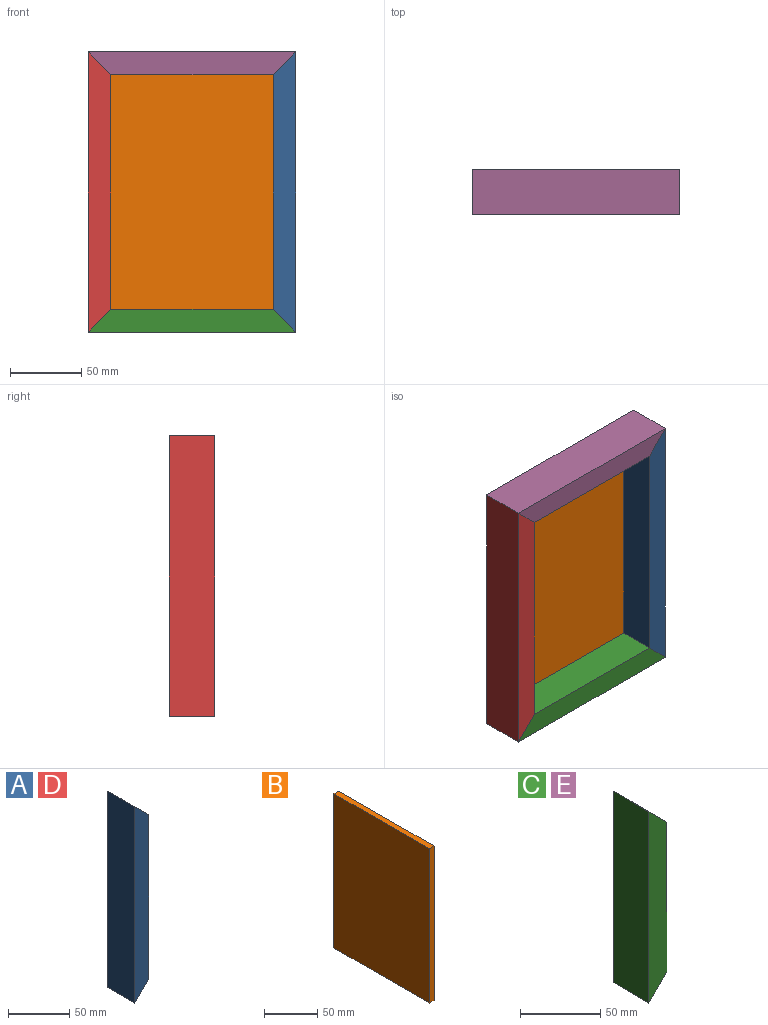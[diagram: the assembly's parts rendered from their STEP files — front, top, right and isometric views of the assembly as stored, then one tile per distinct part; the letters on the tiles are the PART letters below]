
ASSEMBLY  parts=5 mates=4
PART A: 8 faces, bbox 15.9x31.8x196.9 mm
  f0: plane 196.85x15.88mm, normal (0,-1,0), area 2873mm2, adj f1,f5,f6,f7
  f1: plane 165.1x25.4mm, normal (1,0,0), area 4193.5mm2, adj f0,f3,f6,f7
  f2: plane 196.85x9.53mm, normal (0,1,0), area 1784.3mm2, adj f4,f5,f6,f7
  f3: plane 177.8x6.35mm, normal (0,1,0), area 1088.7mm2, adj f1,f4,f6,f7
  f4: plane 177.8x6.35mm, normal (1,0,0), area 1129mm2, adj f2,f3,f6,f7
  f5: plane 196.85x31.75mm, normal (-1,0,0), area 6250mm2, adj f0,f2,f6,f7
  f6: plane 31.75x15.88mm, normal (0.71,0,-0.71), area 655.8mm2, adj f0,f1,f2,f3,f4,f5
  f7: plane 31.75x15.88mm, normal (0.71,0,0.71), area 655.8mm2, adj f0,f1,f2,f3,f4,f5
PART B: 6 faces, bbox 6.4x127x177.8 mm
  f0: plane 177.8x6.35mm, normal (0,1,0), area 1129mm2, adj f1,f3,f4,f5
  f1: plane 127x6.35mm, normal (0,0,1), area 806.5mm2, adj f0,f2,f4,f5
  f2: plane 177.8x6.35mm, normal (0,-1,0), area 1129mm2, adj f1,f3,f4,f5
  f3: plane 127x6.35mm, normal (0,0,-1), area 806.5mm2, adj f0,f2,f4,f5
  f4: plane 177.8x127mm, normal (1,0,0), area 22580.6mm2, adj f0,f1,f2,f3
  f5: plane 177.8x127mm, normal (-1,0,0), area 22580.6mm2, adj f0,f1,f2,f3
PART C: 8 faces, bbox 15.9x31.8x146.1 mm
  f0: plane 146.05x15.88mm, normal (0,-1,0), area 2066.5mm2, adj f1,f5,f6,f7
  f1: plane 114.3x25.4mm, normal (1,0,0), area 2903.2mm2, adj f0,f3,f6,f7
  f2: plane 146.05x9.53mm, normal (0,1,0), area 1300.4mm2, adj f4,f5,f6,f7
  f3: plane 127x6.35mm, normal (0,1,0), area 766.1mm2, adj f1,f4,f6,f7
  f4: plane 127x6.35mm, normal (1,0,0), area 806.5mm2, adj f2,f3,f6,f7
  f5: plane 146.05x31.75mm, normal (-1,0,0), area 4637.1mm2, adj f0,f2,f6,f7
  f6: plane 31.75x15.88mm, normal (0.71,0,-0.71), area 655.8mm2, adj f0,f1,f2,f3,f4,f5
  f7: plane 31.75x15.88mm, normal (0.71,0,0.71), area 655.8mm2, adj f0,f1,f2,f3,f4,f5
PART D: same geometry as A
PART E: same geometry as C
PLACE A rot(axis=(0,1,0),180deg) t=(56.58,6.53,171.96)mm
PLACE B rot(axis=(0,0,-1),90deg) t=(-8.51,22.41,73.53)mm
PLACE C rot(axis=(0,-1,0),90deg) t=(64.52,6.53,-16.95)mm
PLACE D t=(-73.6,6.53,-24.89)mm fixed
PLACE E rot(axis=(0,1,0),90deg) t=(-81.53,6.53,164.02)mm
MATE fastened B.f4 <-> E.f3  axis (0,-1,0) through (-8.51,16.06,162.43)mm
MATE fastened E.f7 <-> A.f6  axis (0.71,0,-0.71) through (56.99,5.43,164.43)mm
MATE fastened C.f7 <-> D.f6  axis (-0.71,0,0.71) through (-74.01,5.43,-17.37)mm
MATE fastened D.f7 <-> E.f6  axis (0.71,0,0.71) through (-74.01,5.43,164.43)mm
